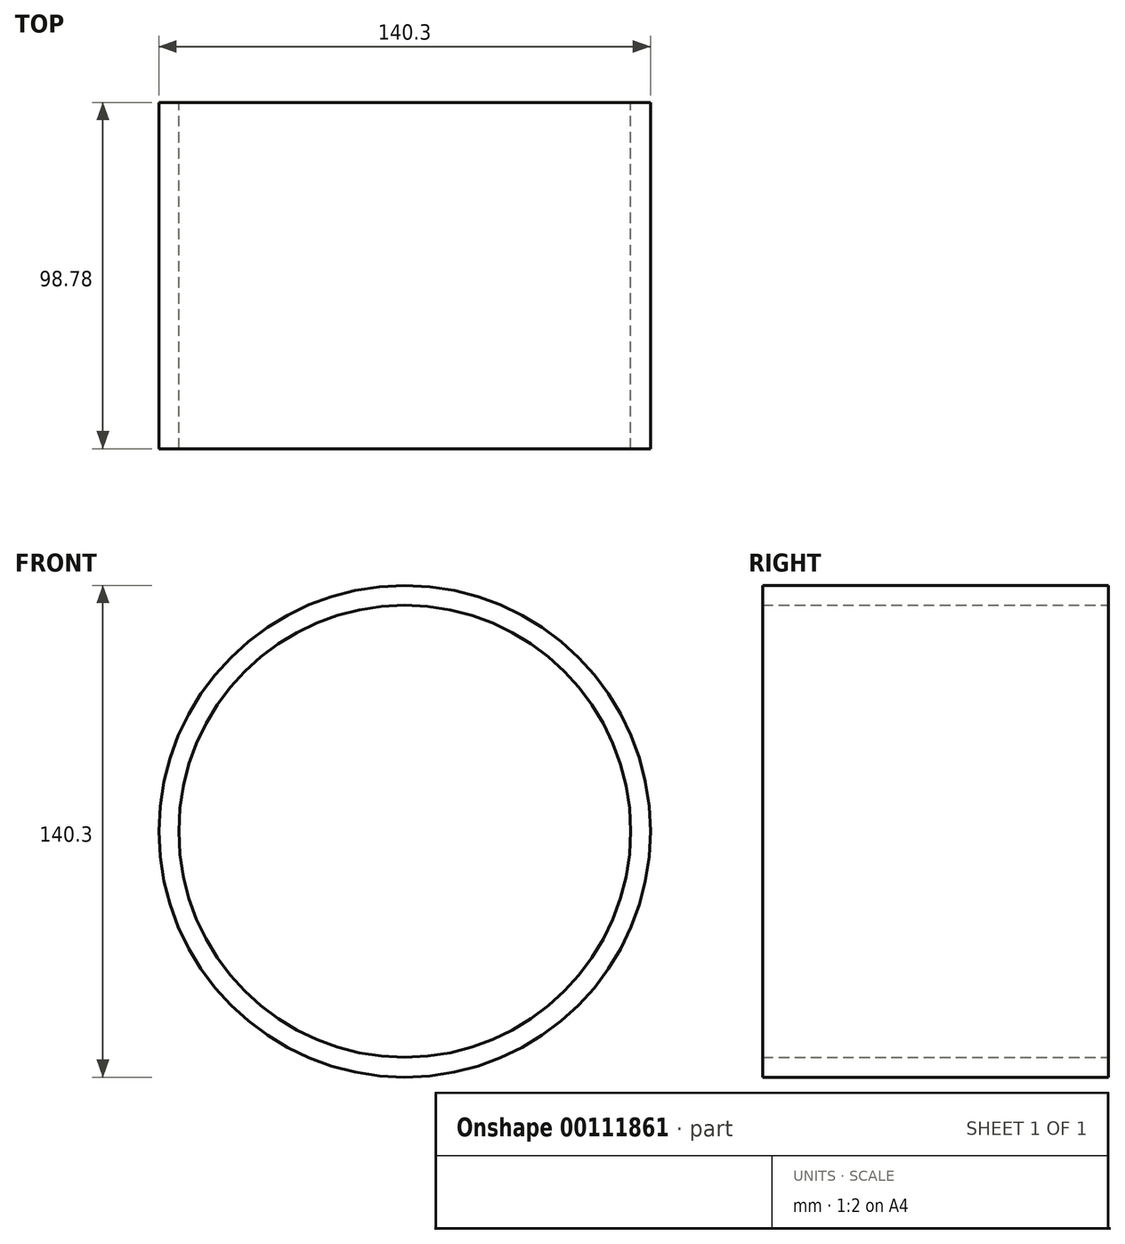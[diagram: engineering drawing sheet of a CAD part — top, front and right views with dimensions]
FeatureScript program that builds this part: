
annotation { "Feature Type Name" : "Feature", "Feature Type Description" : "" }
export const myFeature = defineFeature(function(context is Context, id is Id, definition is map)
    precondition{}
    {
        {
            var Q0;
            Q0=qCreatedBy(makeId("Front.planeOp"),FACE);
            var sketch = newSketch(context, id + "F0", { "sketchPlane" : qUnion([Q0])});
            skCircle(sketch, "E0", {"center": v(0, 0) * mm, "radius": 70.15 * mm});
            skCircle(sketch, "E1", {"center": v(0, 0) * mm, "radius": 64.5 * mm});
            skSolve(sketch);
        }
        {
            var Q0;
            Q0=makeQuery(id+"F0.imprint","IMPRINT",FACE,{"disambiguationData":[TD([[makeQuery(id+"F0.imprint","IMPRINT",EDGE,{"derivedFrom":sQuery(id+"F0.wireOp",EDGE,"E0")}),1.0]])]});
            extrude(context, id + "F1", {"entities" : qUnion([Q0]), "depth" : 98.78 * mm});
        }
    });
